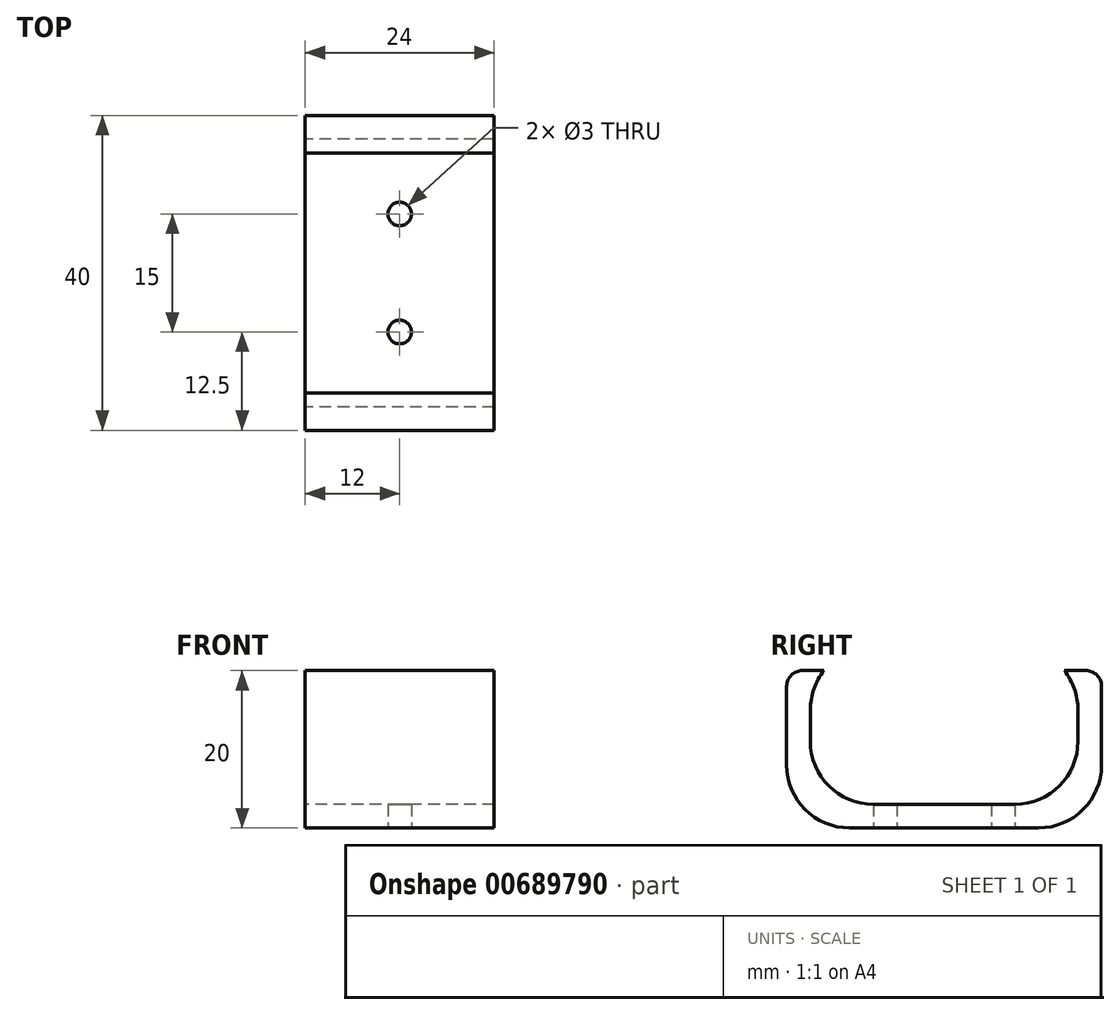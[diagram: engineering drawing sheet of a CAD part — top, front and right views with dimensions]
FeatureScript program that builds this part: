
annotation { "Feature Type Name" : "Feature", "Feature Type Description" : "" }
export const myFeature = defineFeature(function(context is Context, id is Id, definition is map)
    precondition{}
    {
        {
            var Q0;
            Q0=qCreatedBy(makeId("Right.planeOp"),FACE);
            var sketch = newSketch(context, id + "F0", { "sketchPlane" : qUnion([Q0])});
            skLineSegment(sketch, "E0.bottom", {"start": v(8, 0) * mm, "end": v(32, 0) * mm});
            skLineSegment(sketch, "E0.top", {"start": v(2, 20) * mm, "end": v(38, 20) * mm});
            skLineSegment(sketch, "E0.left", {"start": v(0, 8) * mm, "end": v(0, 18) * mm});
            skLineSegment(sketch, "E0.right", {"start": v(40, 8) * mm, "end": v(40, 18) * mm});
            skLineSegment(sketch, "E1.bottom", {"start": v(11, 23) * mm, "end": v(29, 23) * mm});
            skLineSegment(sketch, "E1.top", {"start": v(11, 3) * mm, "end": v(29, 3) * mm});
            skLineSegment(sketch, "E1.left", {"start": v(3, 15) * mm, "end": v(3, 11) * mm});
            skLineSegment(sketch, "E1.right", {"start": v(37, 15) * mm, "end": v(37, 11) * mm});
            skPoint(sketch, "E2.visualSharp", {"position": v(37, 23) * mm});
            skArc(sketch, "E2.filletArc", {"start": v(37, 15) * mm, "mid": v(34.66, 20.66) * mm, "end": v(29, 23) * mm});
            skPoint(sketch, "E3.visualSharp", {"position": v(37, 3) * mm});
            skArc(sketch, "E3.filletArc", {"start": v(29, 3) * mm, "mid": v(34.66, 5.34) * mm, "end": v(37, 11) * mm});
            skPoint(sketch, "E4.visualSharp", {"position": v(3, 3) * mm});
            skArc(sketch, "E4.filletArc", {"start": v(3, 11) * mm, "mid": v(5.34, 5.34) * mm, "end": v(11, 3) * mm});
            skPoint(sketch, "E5.visualSharp", {"position": v(3, 23) * mm});
            skArc(sketch, "E5.filletArc", {"start": v(11, 23) * mm, "mid": v(5.34, 20.66) * mm, "end": v(3, 15) * mm});
            skPoint(sketch, "E6.visualSharp", {"position": v(0, 0) * mm});
            skArc(sketch, "E6.filletArc", {"start": v(0, 8) * mm, "mid": v(2.34, 2.34) * mm, "end": v(8, 0) * mm});
            skPoint(sketch, "E7.visualSharp", {"position": v(40, 0) * mm});
            skArc(sketch, "E7.filletArc", {"start": v(32, 0) * mm, "mid": v(37.66, 2.34) * mm, "end": v(40, 8) * mm});
            skPoint(sketch, "E8.visualSharp", {"position": v(40, 20) * mm});
            skArc(sketch, "E8.filletArc", {"start": v(40, 18) * mm, "mid": v(39.41, 19.41) * mm, "end": v(38, 20) * mm});
            skPoint(sketch, "E9.visualSharp", {"position": v(0, 20) * mm});
            skArc(sketch, "E9.filletArc", {"start": v(2, 20) * mm, "mid": v(0.59, 19.41) * mm, "end": v(0, 18) * mm});
            skSolve(sketch);
        }
        {
            var Q0;
            Q0=makeQuery(id+"F0.imprint","IMPRINT",FACE,{"disambiguationData":[TD([[makeQuery(id+"F0.imprint","IMPRINT",EDGE,{"derivedFrom":sQuery(id+"F0.wireOp",EDGE,"E0.bottom")}),1.0]])]});
            extrude(context, id + "F1", {"entities" : qUnion([Q0]), "depth" : 24 * mm, "offsetDistance" : 25 * mm});
        }
        {
            var Q0;
            Q0=qCreatedBy(makeId("Top.planeOp"),FACE);
            var sketch = newSketch(context, id + "F2", { "sketchPlane" : qUnion([Q0])});
            skCircle(sketch, "E10", {"center": v(12, 12.5) * mm, "radius": 1.5 * mm});
            skCircle(sketch, "E11", {"center": v(12, 27.5) * mm, "radius": 1.5 * mm});
            skSolve(sketch);
        }
        {
            var Q0;
            Q0=makeQuery(id+"F2.imprint","IMPRINT",FACE,{"disambiguationData":[TD([[makeQuery(id+"F2.imprint","IMPRINT",EDGE,{"derivedFrom":sQuery(id+"F2.wireOp",EDGE,"E10")}),1.0]])]});
            var Q1;
            Q1=makeQuery(id+"F2.imprint","IMPRINT",FACE,{"disambiguationData":[TD([[makeQuery(id+"F2.imprint","IMPRINT",EDGE,{"derivedFrom":sQuery(id+"F2.wireOp",EDGE,"E11")}),1.0]])]});
            extrude(context, id + "F3", {"entities" : qUnion([Q0, Q1]), "operationType" : NewBodyOperationType.REMOVE, "depth" : 5 * mm, "offsetDistance" : 25 * mm});
        }
    });
